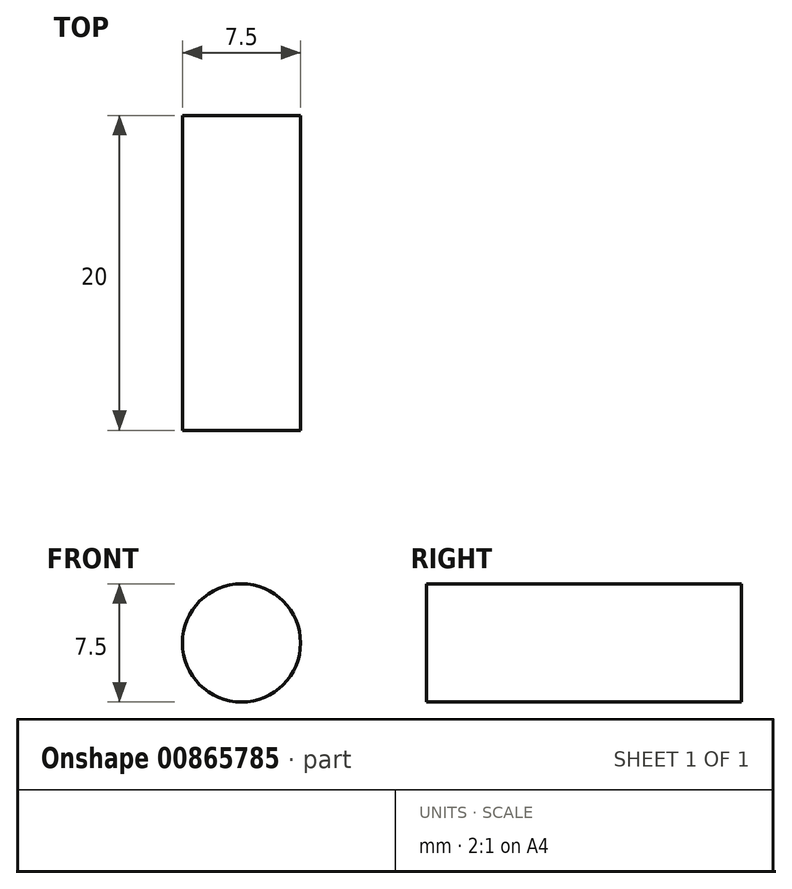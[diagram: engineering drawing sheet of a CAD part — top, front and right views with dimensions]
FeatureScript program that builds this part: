
annotation { "Feature Type Name" : "Feature", "Feature Type Description" : "" }
export const myFeature = defineFeature(function(context is Context, id is Id, definition is map)
    precondition{}
    {
        {
            var Q0;
            Q0=qCreatedBy(makeId("Front.planeOp"),FACE);
            var sketch = newSketch(context, id + "F0", { "sketchPlane" : qUnion([Q0])});
            skCircle(sketch, "E0", {"center": v(0, 0) * mm, "radius": 3.75 * mm});
            skSolve(sketch);
        }
        {
            var Q0;
            Q0=makeQuery(id+"F0.imprint","IMPRINT",FACE,{"disambiguationData":[TD([[makeQuery(id+"F0.imprint","IMPRINT",EDGE,{"derivedFrom":sQuery(id+"F0.wireOp",EDGE,"E0")}),1.0]])]});
            extrude(context, id + "F1", {"entities" : qUnion([Q0]), "depth" : 20 * mm, "offsetDistance" : 25 * mm});
        }
    });
